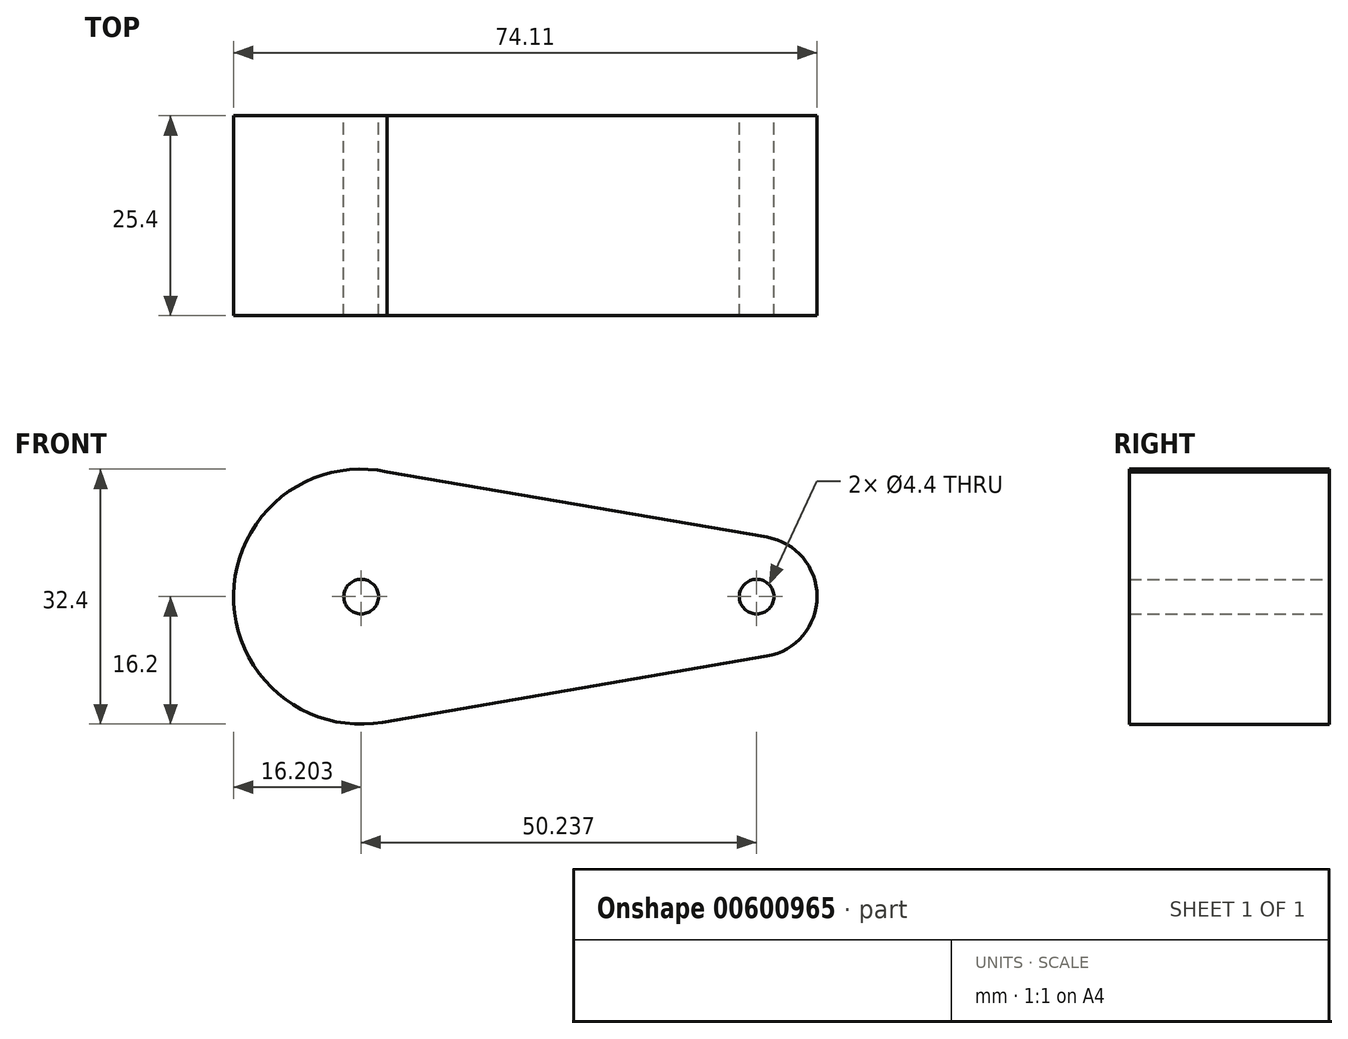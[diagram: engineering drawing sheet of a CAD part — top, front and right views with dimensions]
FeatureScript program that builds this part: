
annotation { "Feature Type Name" : "Feature", "Feature Type Description" : "" }
export const myFeature = defineFeature(function(context is Context, id is Id, definition is map)
    precondition{}
    {
        {
            var Q0;
            Q0=qCreatedBy(makeId("Front.planeOp"),FACE);
            var sketch = newSketch(context, id + "F0", { "sketchPlane" : qUnion([Q0])});
            skCircle(sketch, "E0", {"center": v(-50.24, 0) * mm, "radius": 16.2 * mm});
            skCircle(sketch, "E1", {"center": v(0, 0) * mm, "radius": 7.67 * mm});
            skLineSegment(sketch, "E2", {"start": v(-46.94, 15.86) * mm, "end": v(1.3, 7.56) * mm});
            skLineSegment(sketch, "E3", {"start": v(-47.48, -15.97) * mm, "end": v(1.3, -7.56) * mm});
            skSolve(sketch);
        }
        {
            var Q0;
            {var subQ0=sQuery(id+"F0.wireOp",EDGE,"E0");var subQ1=makeQuery(id+"F0.imprint","INTERSECT",VERTEX,{"derivedFrom":[subQ0,sQuery(id+"F0.wireOp",EDGE,"E2")]});Q0=makeQuery(id+"F0.imprint","IMPRINT",FACE,{"disambiguationData":[TD([[makeQuery(id+"F0.imprint","IMPRINT",EDGE,{"disambiguationData":[TD([[subQ1,-1.0]])],"derivedFrom":subQ0}),1.0]])]});}
            var Q1;
            {var subQ0=sQuery(id+"F0.wireOp",EDGE,"E2");Q1=makeQuery(id+"F0.imprint","IMPRINT",FACE,{"disambiguationData":[TD([[makeQuery(id+"F0.imprint","IMPRINT",EDGE,{"derivedFrom":subQ0}),-1.0]])]});}
            var Q2;
            {var subQ0=sQuery(id+"F0.wireOp",EDGE,"E1");var subQ1=makeQuery(id+"F0.imprint","INTERSECT",VERTEX,{"derivedFrom":[subQ0,sQuery(id+"F0.wireOp",EDGE,"E2")]});Q2=makeQuery(id+"F0.imprint","IMPRINT",FACE,{"disambiguationData":[TD([[makeQuery(id+"F0.imprint","IMPRINT",EDGE,{"disambiguationData":[TD([[subQ1,-1.0]])],"derivedFrom":subQ0}),1.0]])]});}
            var Q3;
            {var subQ0=sQuery(id+"F0.wireOp",EDGE,"E1");var subQ1=makeQuery(id+"F0.imprint","INTERSECT",VERTEX,{"derivedFrom":[subQ0,sQuery(id+"F0.wireOp",EDGE,"E2")]});Q3=makeQuery(id+"F0.imprint","IMPRINT",FACE,{"disambiguationData":[TD([[makeQuery(id+"F0.imprint","IMPRINT",EDGE,{"disambiguationData":[TD([[subQ1,-1.0]])],"derivedFrom":subQ0}),1.0]])]});}
            extrude(context, id + "F1", {"entities" : qUnion([Q0, Q1, Q2, Q3]), "depth" : 25.4 * mm, "offsetDistance" : 25.4 * mm});
        }
        {
            var Q0;
            Q0=sQuery(id+"F0.wireOp",VERTEX,"E0.center");
            var Q1;
            Q1=sQuery(id+"F0.wireOp",VERTEX,"E1.center");
            var Q2;
            Q2=makeQuery(id+"F1.opExtrude","SWEPT_BODY",BODY,{"disambiguationData":[OSD([sQuery(id+"F0.wireOp",EDGE,"E0"),sQuery(id+"F0.wireOp",EDGE,"E1"),sQuery(id+"F0.wireOp",EDGE,"E2"),sQuery(id+"F0.wireOp",EDGE,"E3")])]});
            hole(context, id + "F2", {"style" : HoleStyle.SIMPLE, "endStyle" : HoleEndStyle.THROUGH, "oppositeDirection" : true, "holeDiameter" : 4.4 * mm, "majorDiameter" : 6.35 * mm, "isTappedThrough" : true, "tappedDepth" : 12.7 * mm, "tapClearance" : 3, "startFromSketch" : true, "locations" : qUnion([Q0, Q1]), "scope" : qUnion([Q2])});
        }
    });
